# Revit family: Electrical_Controls_Conspec_CN-Series-Fixed-Gas-Detector
name_source: partatom
category: Electrical Fixtures
units: mm (PartAtom-declared; Revit-internal decimal feet)

## family parameters
Classification Number = 23.85.30.21
Cut with Voids When Loaded = No
Host = Face
Maintain Annotation Orientation = No
Part Type = Normal
Room Calculation Point = No
Round Connector Dimension = Use Diameter
Shared = No

## types (13) — shared parameters
Apparent Load = 0 VA
Assembly Code = D5030
Cable Requirements = 3-Conductor 18 AWG Suggested
Current Consumption = 50 mA
Date Updated = 2023/10/17
Depth = 2.97 "
Description = CN Series Fixed Gas Detector
Display = 2 line, 8 character Alphanumeric LCD
Enclosure Rating and Finish = NEMA 4X
Frequency = 0 Hz
Height = 2.95 "
Keynote = 16000
Manufacturer = CONSPEC Controls
Models = 2 (Calibration & Normal)
Number of Poles = 3
Operating Humidity = 10% to 90% RH Non-Condesing
Operating Temperature = -4°F to +120°F
Output Signal = Linear 4-20mA
Power Factor = 0.8
Product Material = Conspec - Plastic - FR ABS - Grey
Product data url = https://bimobject.com
Sensory Types = Electrochemical, Catalytic Bead, Infrared, Photo-Ionization, Thermal Conductivity
URL = https://www.conspec-controls.com
Version = 1
Voltage = 24 V
Voltage Range = 12V - 24V DC
Weight = 3.00 lbf
Width = 4.33 "
zero-valued in all types: Default Elevation

## per-type parameters (varying)
| type | Gas Detecting | Model |
| CN – Sulfur Dioxide | Sulfur Dioxide | CN13 |
| CN – Ozone | Ozone | CN12 |
| CN – Oxygen | Oxygen | CN11 |
| CN – Nitrogen Dioxide | Nitrogen Dioxide | CN10 |
| CN – Nitric Oxide | Nitric Oxide | CN09 |
| CN – Hydrogen Sulfide | Hydrogen Sulfide | CN08 |
| CN – Hydrogen Chloride | Hydrogen Chloride | CN07 |
| CN – Hydrogen | Hydrogen | CN06 |
| CN – Combustibles | Combustibles | CN05 |
| CN – Chlorine | Chlorine | CN04 |
| CN – Carbon Monoxide | Carbon Monoxide | CN03 |
| CN – Carbon Dioxide | Carbon Dioxide | CN02 |
| CN – Ammonia | Ammonia | CN01 |

## geometry (parser evidence)
native form markers: Sweep x3
no freeform markers — native parametric forms only
